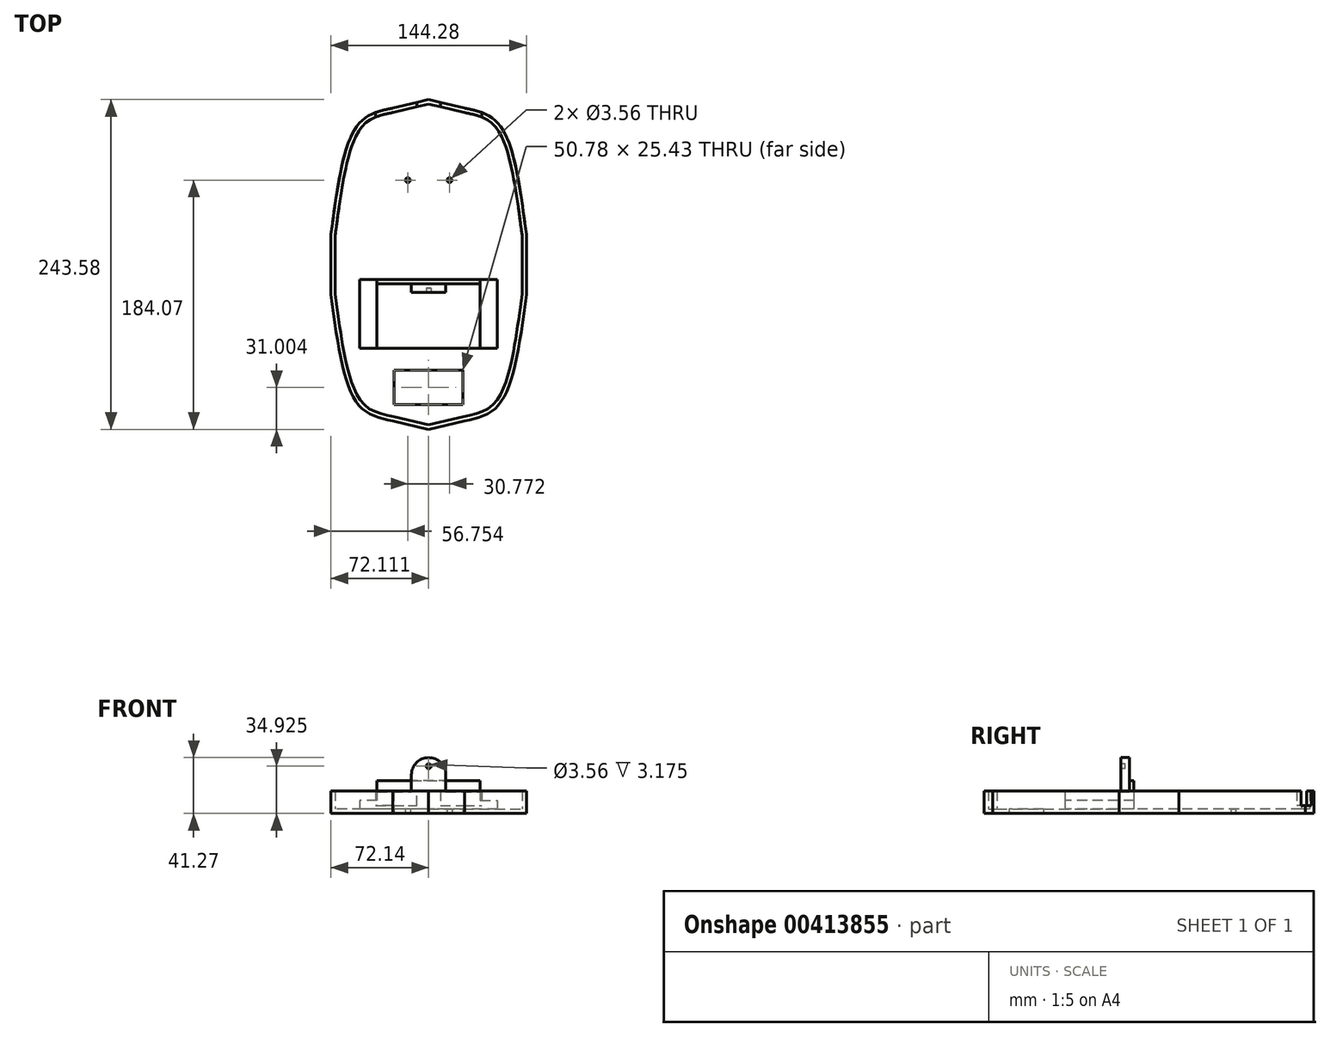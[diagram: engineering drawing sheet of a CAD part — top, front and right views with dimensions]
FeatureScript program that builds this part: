
annotation { "Feature Type Name" : "Feature", "Feature Type Description" : "" }
export const myFeature = defineFeature(function(context is Context, id is Id, definition is map)
    precondition{}
    {
        {
            var Q0;
            Q0=qCreatedBy(makeId("Top.planeOp"),FACE);
            cPlane(context, id + "F0", {"entities" : qUnion([Q0]), "cplaneType" : CPlaneType.OFFSET, "offset" : 53.97 * mm, "width" : 152.4 * mm, "height" : 152.4 * mm});
        }
        {
            var Q0;
            Q0=qCreatedBy(makeId("Top.planeOp"),FACE);
            cPlane(context, id + "F1", {"entities" : qUnion([Q0]), "cplaneType" : CPlaneType.OFFSET, "offset" : 120.65 * mm, "width" : 152.4 * mm, "height" : 152.4 * mm});
        }
        {
            var Q0;
            Q0=qCreatedBy(id+"F1.planeOp",FACE);
            var sketch = newSketch(context, id + "F2", { "sketchPlane" : qUnion([Q0])});
            skLineSegment(sketch, "E0", {"start": v(0, 121.8) * mm, "end": v(26.48, 115.52) * mm});
            skFitSpline(sketch, "E1", {"points": [v(26.48, 115.52) * mm, v(46, 108.9) * mm, v(59.94, 88) * mm, v(72.14, 22.13) * mm], "startDerivative": vector(81.9, -17.1) * mm, "endDerivative": vector(21.27, -161.05) * mm});
            skLineSegment(sketch, "E2", {"start": v(72.14, 22.13) * mm, "end": v(72.14, 0) * mm});
            skLineSegment(sketch, "E3.MirrorCS", {"start": v(0, 121.8) * mm, "end": v(-26.48, 115.52) * mm});
            skFitSpline(sketch, "E4.MirrorCS", {"points": [v(-26.48, 115.52) * mm, v(-46, 108.9) * mm, v(-59.94, 88) * mm, v(-72.14, 22.13) * mm], "startDerivative": vector(-81.9, -17.1) * mm, "endDerivative": vector(-21.27, -161.05) * mm});
            skLineSegment(sketch, "E5.MirrorCS", {"start": v(-72.14, 22.13) * mm, "end": v(-72.14, 0) * mm});
            skLineSegment(sketch, "E6.MirrorCS", {"start": v(72.14, -22.13) * mm, "end": v(72.14, 0) * mm});
            skFitSpline(sketch, "E7.MirrorCS", {"points": [v(26.48, -115.52) * mm, v(46, -108.9) * mm, v(59.94, -88) * mm, v(72.14, -22.13) * mm], "startDerivative": vector(81.9, 17.1) * mm, "endDerivative": vector(21.27, 161.05) * mm});
            skLineSegment(sketch, "E8.MirrorCS", {"start": v(0, -121.8) * mm, "end": v(26.48, -115.52) * mm});
            skLineSegment(sketch, "E9.MirrorCS", {"start": v(0, -121.8) * mm, "end": v(-26.48, -115.52) * mm});
            skFitSpline(sketch, "E10.MirrorCS", {"points": [v(-26.48, -115.52) * mm, v(-46, -108.9) * mm, v(-59.94, -88) * mm, v(-72.14, -22.13) * mm], "startDerivative": vector(-81.9, 17.1) * mm, "endDerivative": vector(-21.27, 161.05) * mm});
            skLineSegment(sketch, "E11.MirrorCS", {"start": v(-72.14, -22.13) * mm, "end": v(-72.14, 0) * mm});
            skSolve(sketch);
        }
        {
            var Q0;
            Q0=qCreatedBy(id+"F1.planeOp",FACE);
            var sketch = newSketch(context, id + "F3", { "sketchPlane" : qUnion([Q0])});
            skCircle(sketch, "E12", {"center": v(-15.39, 62.28) * mm, "radius": 1.78 * mm});
            skLineSegment(sketch, "E13", {"start": v(0, 70.65) * mm, "end": v(0, 64.35) * mm});
            skCircle(sketch, "E14.MirrorC", {"center": v(15.39, 62.28) * mm, "radius": 1.78 * mm});
            skLineSegment(sketch, "E15.bottom", {"start": v(-25.42, -103.5) * mm, "end": v(25.36, -103.5) * mm});
            skLineSegment(sketch, "E15.top", {"start": v(-25.42, -78.07) * mm, "end": v(25.36, -78.07) * mm});
            skLineSegment(sketch, "E15.left", {"start": v(-25.42, -103.5) * mm, "end": v(-25.42, -78.07) * mm});
            skLineSegment(sketch, "E15.right", {"start": v(25.36, -103.5) * mm, "end": v(25.36, -78.07) * mm});
            skSolve(sketch);
        }
        {
            var Q0;
            Q0=makeQuery(id+"F2.imprint","IMPRINT",FACE,{"disambiguationData":[TD([[makeQuery(id+"F2.imprint","IMPRINT",EDGE,{"derivedFrom":sQuery(id+"F2.wireOp",EDGE,"E3.MirrorCS")}),1.0]])]});
            var Q1;
            Q1=makeQuery(id+"F2.imprint","IMPRINT",FACE,{"disambiguationData":[TD([[makeQuery(id+"F2.imprint","IMPRINT",EDGE,{"derivedFrom":sQuery(id+"F2.wireOp",EDGE,"E0")}),-1.0]])]});
            var Q2;
            Q2=makeQuery(id+"F2.imprint","IMPRINT",FACE,{"disambiguationData":[TD([[makeQuery(id+"F2.imprint","IMPRINT",EDGE,{"derivedFrom":sQuery(id+"F2.wireOp",EDGE,"E6.MirrorCS")}),1.0]])]});
            var Q3;
            Q3=makeQuery(id+"F2.imprint","IMPRINT",FACE,{"disambiguationData":[TD([[makeQuery(id+"F2.imprint","IMPRINT",EDGE,{"derivedFrom":sQuery(id+"F2.wireOp",EDGE,"E9.MirrorCS")}),-1.0]])]});
            extrude(context, id + "F4", {"entities" : qUnion([Q0, Q1, Q2, Q3]), "depth" : 16.76 * mm});
        }
        {
            var Q0;
            Q0=makeQuery(id+"F4.opExtrude","CAP_FACE",FACE,{"disambiguationData":[OSD([sQuery(id+"F2.wireOp",EDGE,"E0"),sQuery(id+"F2.wireOp",EDGE,"E1"),sQuery(id+"F2.wireOp",EDGE,"E2"),sQuery(id+"F2.wireOp",EDGE,"E3.MirrorCS"),sQuery(id+"F2.wireOp",EDGE,"E4.MirrorCS"),sQuery(id+"F2.wireOp",EDGE,"E5.MirrorCS"),sQuery(id+"F2.wireOp",EDGE,"E6.MirrorCS"),sQuery(id+"F2.wireOp",EDGE,"E7.MirrorCS"),sQuery(id+"F2.wireOp",EDGE,"E8.MirrorCS"),sQuery(id+"F2.wireOp",EDGE,"E9.MirrorCS"),sQuery(id+"F2.wireOp",EDGE,"E10.MirrorCS"),sQuery(id+"F2.wireOp",EDGE,"E11.MirrorCS")])],"isStart":false});
            shell(context, id + "F5", {"entities" : qUnion([Q0]), "thickness" : 3.17 * mm});
        }
        {
            var Q0;
            Q0 = qSketchRegion(id + "F3", true);
            extrude(context, id + "F6", {"entities" : qUnion([Q0]), "operationType" : NewBodyOperationType.REMOVE, "depth" : 25.4 * mm});
        }
        {
            var Q0;
            Q0=makeQuery(id+"F5.opShell","OFFSET_FACE",FACE,{"disambiguationData":[OSD([sQuery(id+"F2.wireOp",EDGE,"E0"),sQuery(id+"F2.wireOp",EDGE,"E1"),sQuery(id+"F2.wireOp",EDGE,"E2"),sQuery(id+"F2.wireOp",EDGE,"E3.MirrorCS"),sQuery(id+"F2.wireOp",EDGE,"E4.MirrorCS"),sQuery(id+"F2.wireOp",EDGE,"E5.MirrorCS"),sQuery(id+"F2.wireOp",EDGE,"E6.MirrorCS"),sQuery(id+"F2.wireOp",EDGE,"E7.MirrorCS"),sQuery(id+"F2.wireOp",EDGE,"E8.MirrorCS"),sQuery(id+"F2.wireOp",EDGE,"E9.MirrorCS"),sQuery(id+"F2.wireOp",EDGE,"E10.MirrorCS"),sQuery(id+"F2.wireOp",EDGE,"E11.MirrorCS")])]});
            var sketch = newSketch(context, id + "F7", { "sketchPlane" : qUnion([Q0])});
            skLineSegment(sketch, "E16.bottom", {"start": v(38.1, -11.21) * mm, "end": v(-38.1, -11.21) * mm});
            skLineSegment(sketch, "E16.top", {"start": v(38.1, -62.01) * mm, "end": v(-38.1, -62.01) * mm});
            skLineSegment(sketch, "E16.left", {"start": v(38.1, -11.21) * mm, "end": v(38.1, -62.01) * mm});
            skLineSegment(sketch, "E16.right", {"start": v(-38.1, -11.21) * mm, "end": v(-38.1, -62.01) * mm});
            skPoint(sketch, "E16.middle", {"position": v(0, -36.61) * mm});
            skSolve(sketch);
        }
        {
            var Q0;
            Q0 = qSketchRegion(id + "F7", true);
            extrude(context, id + "F8", {"entities" : qUnion([Q0]), "operationType" : NewBodyOperationType.ADD, "depth" : 12.7 * mm});
        }
        {
            var Q0;
            Q0=makeQuery(id+"F5.opShell","OFFSET_FACE",FACE,{"disambiguationData":[OSD([sQuery(id+"F2.wireOp",EDGE,"E0"),sQuery(id+"F2.wireOp",EDGE,"E1"),sQuery(id+"F2.wireOp",EDGE,"E2"),sQuery(id+"F2.wireOp",EDGE,"E3.MirrorCS"),sQuery(id+"F2.wireOp",EDGE,"E4.MirrorCS"),sQuery(id+"F2.wireOp",EDGE,"E5.MirrorCS"),sQuery(id+"F2.wireOp",EDGE,"E6.MirrorCS"),sQuery(id+"F2.wireOp",EDGE,"E7.MirrorCS"),sQuery(id+"F2.wireOp",EDGE,"E8.MirrorCS"),sQuery(id+"F2.wireOp",EDGE,"E9.MirrorCS"),sQuery(id+"F2.wireOp",EDGE,"E10.MirrorCS"),sQuery(id+"F2.wireOp",EDGE,"E11.MirrorCS")])]});
            var sketch = newSketch(context, id + "F9", { "sketchPlane" : qUnion([Q0])});
            skLineSegment(sketch, "E17.bottom", {"start": v(-38.1, -11.21) * mm, "end": v(-50.8, -11.21) * mm});
            skLineSegment(sketch, "E17.top", {"start": v(-38.1, -62.01) * mm, "end": v(-50.8, -62.01) * mm});
            skLineSegment(sketch, "E17.left", {"start": v(-38.1, -11.21) * mm, "end": v(-38.1, -62.01) * mm});
            skLineSegment(sketch, "E17.right", {"start": v(-50.8, -11.21) * mm, "end": v(-50.8, -62.01) * mm});
            skLineSegment(sketch, "E18.bottom", {"start": v(38.1, -11.21) * mm, "end": v(50.8, -11.21) * mm});
            skLineSegment(sketch, "E18.top", {"start": v(38.1, -62.01) * mm, "end": v(50.8, -62.01) * mm});
            skLineSegment(sketch, "E18.left", {"start": v(38.1, -11.21) * mm, "end": v(38.1, -62.01) * mm});
            skLineSegment(sketch, "E18.right", {"start": v(50.8, -11.21) * mm, "end": v(50.8, -62.01) * mm});
            skSolve(sketch);
        }
        {
            var Q0;
            Q0 = qSketchRegion(id + "F9", true);
            extrude(context, id + "F10", {"entities" : qUnion([Q0]), "operationType" : NewBodyOperationType.ADD, "depth" : 6.35 * mm});
        }
        {
            var Q0;
            Q0=makeQuery(id+"F8.opExtrude","CAP_FACE",FACE,{"disambiguationData":[OSD([sQuery(id+"F7.wireOp",EDGE,"E16.bottom"),sQuery(id+"F7.wireOp",EDGE,"E16.top"),sQuery(id+"F7.wireOp",EDGE,"E16.left"),sQuery(id+"F7.wireOp",EDGE,"E16.right")])],"isStart":false});
            var sketch = newSketch(context, id + "F11", { "sketchPlane" : qUnion([Q0])});
            skLineSegment(sketch, "E19.bottom", {"start": v(-38.1, -11.21) * mm, "end": v(38.1, -11.21) * mm});
            skLineSegment(sketch, "E19.top", {"start": v(-38.1, -14.39) * mm, "end": v(38.1, -14.39) * mm});
            skLineSegment(sketch, "E19.left", {"start": v(-38.1, -11.21) * mm, "end": v(-38.1, -14.39) * mm});
            skLineSegment(sketch, "E19.right", {"start": v(38.1, -11.21) * mm, "end": v(38.1, -14.39) * mm});
            skSolve(sketch);
        }
        {
            var Q0;
            Q0 = qSketchRegion(id + "F11", true);
            extrude(context, id + "F12", {"entities" : qUnion([Q0]), "operationType" : NewBodyOperationType.ADD, "depth" : 8.38 * mm});
        }
        {
            var Q0;
            Q0=makeQuery(id+"F8.opExtrude","CAP_FACE",FACE,{"disambiguationData":[OSD([sQuery(id+"F7.wireOp",EDGE,"E16.bottom"),sQuery(id+"F7.wireOp",EDGE,"E16.top"),sQuery(id+"F7.wireOp",EDGE,"E16.left"),sQuery(id+"F7.wireOp",EDGE,"E16.right")])],"isStart":false});
            var sketch = newSketch(context, id + "F13", { "sketchPlane" : qUnion([Q0])});
            skLineSegment(sketch, "E20.bottom", {"start": v(12.7, -20.74) * mm, "end": v(-12.7, -20.74) * mm});
            skLineSegment(sketch, "E20.left", {"start": v(12.7, -20.74) * mm, "end": v(12.7, -14.39) * mm});
            skLineSegment(sketch, "E20.right", {"start": v(-12.7, -20.74) * mm, "end": v(-12.7, -14.39) * mm});
            skPoint(sketch, "E20.middle", {"position": v(0, -14.39) * mm});
            skLineSegment(sketch, "E21", {"start": v(-12.7, -14.39) * mm, "end": v(12.7, -14.39) * mm});
            skPoint(sketch, "E20.top.end.orphan", {"position": v(-12.7, -8.03) * mm});
            skPoint(sketch, "E22.orphan", {"position": v(12.7, -8.03) * mm});
            skSolve(sketch);
        }
        {
            var Q0;
            Q0 = qSketchRegion(id + "F13", true);
            extrude(context, id + "F14", {"entities" : qUnion([Q0]), "operationType" : NewBodyOperationType.ADD, "depth" : 25.4 * mm});
        }
        {
            var Q0;
            Q0=makeQuery(id+"F14.opExtrude","CAP_EDGE",EDGE,{"disambiguationData":[OSD([sQuery(id+"F13.wireOp",EDGE,"E20.right")])],"isStart":false});
            var Q1;
            Q1=makeQuery(id+"F14.opExtrude","CAP_EDGE",EDGE,{"disambiguationData":[OSD([sQuery(id+"F13.wireOp",EDGE,"E20.left")])],"isStart":false});
            fillet(context, id + "F15", {"entities" : qUnion([Q0, Q1]), "radius" : 12.7 * mm, "tangentPropagation" : true, "allowEdgeOverflow" : false});
        }
        {
            var Q0;
            Q0=makeQuery(id+"F14.opExtrude","SWEPT_FACE",FACE,{"disambiguationData":[OSD([sQuery(id+"F13.wireOp",EDGE,"E20.bottom")])]});
            var sketch = newSketch(context, id + "F16", { "sketchPlane" : qUnion([Q0])});
            skLineSegment(sketch, "E23", {"start": v(0, 161.93) * mm, "end": v(0, 155.58) * mm});
            skPoint(sketch, "E23.endSnap0", {"position": v(0, 161.93) * mm});
            skCircle(sketch, "E24", {"center": v(0, 155.58) * mm, "radius": 1.78 * mm});
            skSolve(sketch);
        }
        {
            var Q0;
            Q0=makeQuery(id+"F16.imprint","IMPRINT",FACE,{"disambiguationData":[TD([[makeQuery(id+"F16.imprint","IMPRINT",EDGE,{"derivedFrom":sQuery(id+"F16.wireOp",EDGE,"E24")}),1.0]])]});
            extrude(context, id + "F17", {"entities" : qUnion([Q0]), "operationType" : NewBodyOperationType.REMOVE, "oppositeDirection" : true, "depth" : 3.17 * mm});
        }
        {
            var Q0;
            Q0=makeQuery(id+"F12.boolean.opBoolean","MERGE",FACE,{"derivedFrom":[makeQuery(id+"F10.boolean.opBoolean","MERGE",FACE,{"derivedFrom":[makeQuery(id+"F8.opExtrude","SWEPT_FACE",FACE,{"disambiguationData":[OSD([sQuery(id+"F7.wireOp",EDGE,"E16.bottom")])]}),makeQuery(id+"F10.opExtrude","SWEPT_FACE",FACE,{"disambiguationData":[OSD([sQuery(id+"F9.wireOp",EDGE,"E17.bottom")])]}),makeQuery(id+"F10.opExtrude","SWEPT_FACE",FACE,{"disambiguationData":[OSD([sQuery(id+"F9.wireOp",EDGE,"E18.bottom")])]})]}),makeQuery(id+"F12.opExtrude","SWEPT_FACE",FACE,{"disambiguationData":[OSD([sQuery(id+"F11.wireOp",EDGE,"E19.bottom")])]})]});
            var sketch = newSketch(context, id + "F18", { "sketchPlane" : qUnion([Q0])});
            skLineSegment(sketch, "E25", {"start": v(-8.7, 126.37) * mm, "end": v(-8.7, 143.59) * mm});
            skLineSegment(sketch, "E26", {"start": v(-8.7, 143.59) * mm, "end": v(-39.19, 143.59) * mm});
            skLineSegment(sketch, "E27", {"start": v(-39.19, 143.59) * mm, "end": v(-39.19, 126.37) * mm});
            skLineSegment(sketch, "E28", {"start": v(0, 126.37) * mm, "end": v(0, 142.68) * mm});
            skPoint(sketch, "E28.endSnap0", {"position": v(0, 126.37) * mm});
            skLineSegment(sketch, "E29", {"start": v(-39.19, 126.37) * mm, "end": v(-8.7, 126.37) * mm});
            skLineSegment(sketch, "E30.MirrorCS", {"start": v(8.7, 143.59) * mm, "end": v(39.19, 143.59) * mm});
            skLineSegment(sketch, "E31.MirrorCS", {"start": v(8.7, 126.37) * mm, "end": v(8.7, 143.59) * mm});
            skLineSegment(sketch, "E32.MirrorCS", {"start": v(39.19, 126.37) * mm, "end": v(8.7, 126.37) * mm});
            skLineSegment(sketch, "E33.MirrorCS", {"start": v(39.19, 143.59) * mm, "end": v(39.19, 126.37) * mm});
            skLineSegment(sketch, "E34", {"start": v(0, 126.37) * mm, "end": v(0, 128.9) * mm});
            skLineSegment(sketch, "E35", {"start": v(0, 126.37) * mm, "end": v(-19.9, 126.37) * mm});
            skSolve(sketch);
        }
        {
            var Q0;
            Q0 = qSketchRegion(id + "F18", true);
            extrude(context, id + "F19", {"entities" : qUnion([Q0]), "operationType" : NewBodyOperationType.REMOVE, "depth" : 170.94 * mm});
        }
    });
